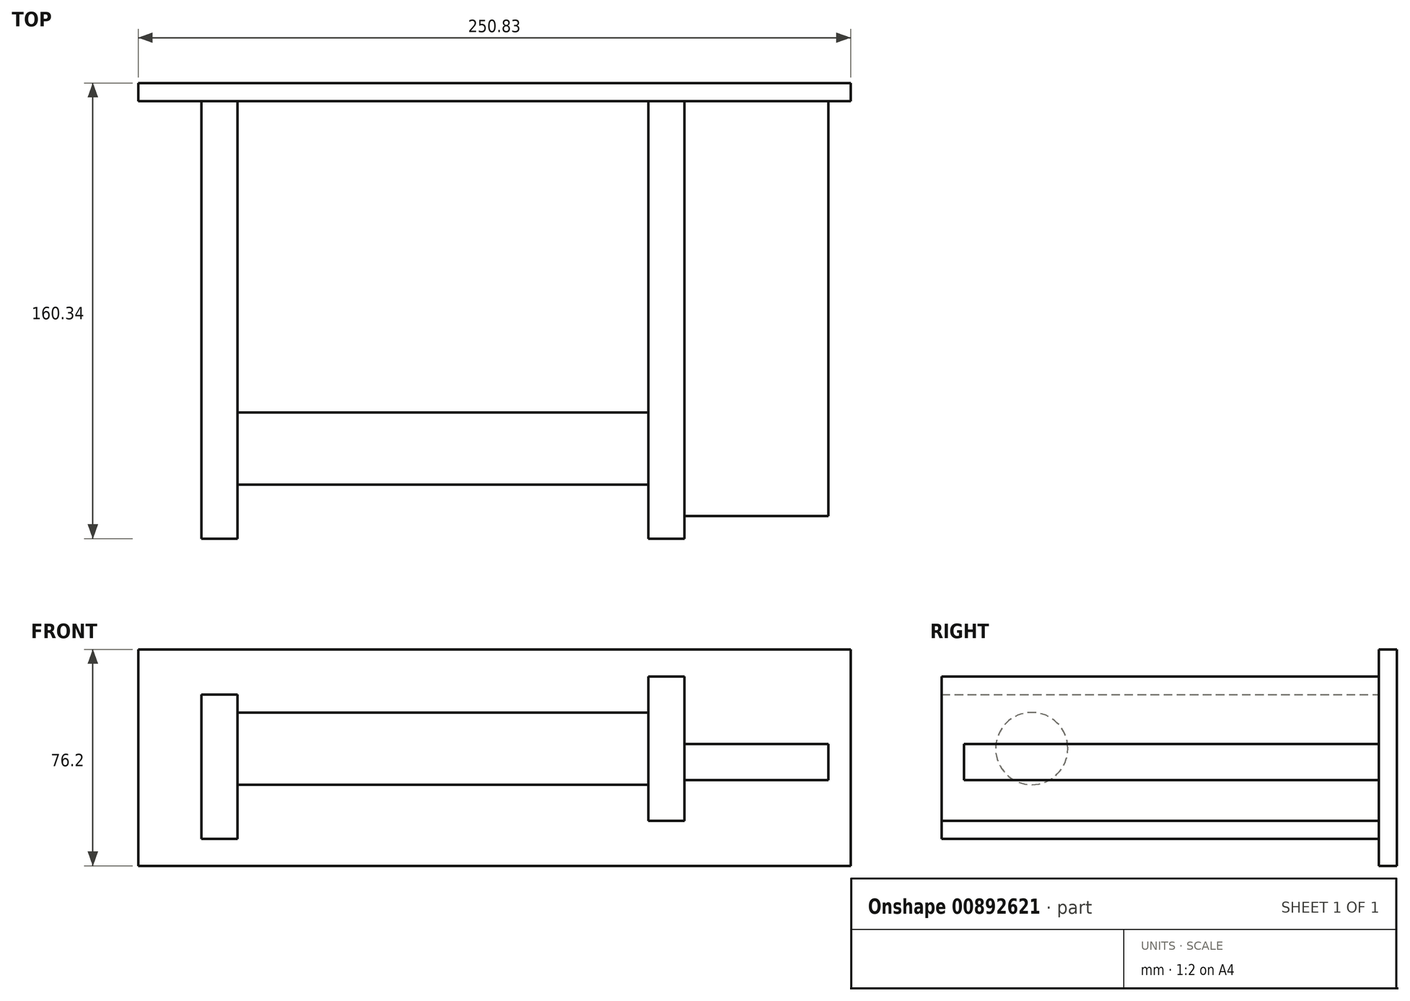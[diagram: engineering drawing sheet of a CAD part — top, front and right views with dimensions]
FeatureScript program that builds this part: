
annotation { "Feature Type Name" : "Feature", "Feature Type Description" : "" }
export const myFeature = defineFeature(function(context is Context, id is Id, definition is map)
    precondition{}
    {
        {
            var Q0;
            Q0=qCreatedBy(makeId("Front.planeOp"),FACE);
            var sketch = newSketch(context, id + "F0", { "sketchPlane" : qUnion([Q0])});
            skLineSegment(sketch, "E0.bottom", {"start": v(-131.88, 15.88) * mm, "end": v(118.95, 15.88) * mm});
            skLineSegment(sketch, "E0.top", {"start": v(-131.88, -60.33) * mm, "end": v(118.95, -60.33) * mm});
            skLineSegment(sketch, "E0.left", {"start": v(-131.88, 15.88) * mm, "end": v(-131.88, -60.33) * mm});
            skLineSegment(sketch, "E0.right", {"start": v(118.95, 15.88) * mm, "end": v(118.95, -60.33) * mm});
            skLineSegment(sketch, "E1.bottom", {"start": v(-109.65, -50.8) * mm, "end": v(-96.95, -50.8) * mm});
            skLineSegment(sketch, "E1.top", {"start": v(-109.65, 0) * mm, "end": v(-96.95, 0) * mm});
            skLineSegment(sketch, "E1.left", {"start": v(-109.65, -50.8) * mm, "end": v(-109.65, 0) * mm});
            skLineSegment(sketch, "E1.right", {"start": v(-96.95, -50.8) * mm, "end": v(-96.95, 0) * mm});
            skSolve(sketch);
        }
        {
            var Q0;
            Q0=makeQuery(id+"F0.imprint","IMPRINT",FACE,{"disambiguationData":[TD([[makeQuery(id+"F0.imprint","IMPRINT",EDGE,{"derivedFrom":sQuery(id+"F0.wireOp",EDGE,"E0.bottom")}),-1.0]])]});
            extrude(context, id + "F1", {"entities" : qUnion([Q0]), "depth" : 6.35 * mm, "offsetDistance" : 25.4 * mm});
        }
        {
            var Q0;
            Q0=makeQuery(id+"F0.imprint","IMPRINT",FACE,{"disambiguationData":[TD([[makeQuery(id+"F0.imprint","IMPRINT",EDGE,{"derivedFrom":sQuery(id+"F0.wireOp",EDGE,"E1.bottom")}),1.0]])]});
            extrude(context, id + "F2", {"entities" : qUnion([Q0]), "operationType" : NewBodyOperationType.ADD, "depth" : 160.34 * mm, "offsetDistance" : 25.4 * mm});
        }
        {
            var Q0;
            Q0=qCreatedBy(makeId("Front.planeOp"),FACE);
            var sketch = newSketch(context, id + "F3", { "sketchPlane" : qUnion([Q0])});
            skLineSegment(sketch, "E2.bottom", {"start": v(47.68, -44.45) * mm, "end": v(60.38, -44.45) * mm});
            skLineSegment(sketch, "E2.top", {"start": v(47.68, 6.35) * mm, "end": v(60.38, 6.35) * mm});
            skLineSegment(sketch, "E2.left", {"start": v(47.68, -44.45) * mm, "end": v(47.68, 6.35) * mm});
            skLineSegment(sketch, "E2.right", {"start": v(60.38, -44.45) * mm, "end": v(60.38, 6.35) * mm});
            skSolve(sketch);
        }
        {
            var Q0;
            Q0=qSketchRegion(id+"F3",true);
            extrude(context, id + "F4", {"entities" : qUnion([Q0]), "operationType" : NewBodyOperationType.ADD, "depth" : 160.34 * mm, "offsetDistance" : 25.4 * mm});
        }
        {
            var Q0;
            Q0=qCreatedBy(makeId("Front.planeOp"),FACE);
            var sketch = newSketch(context, id + "F5", { "sketchPlane" : qUnion([Q0])});
            skLineSegment(sketch, "E3.bottom", {"start": v(111.07, -30.09) * mm, "end": v(60.27, -30.09) * mm});
            skLineSegment(sketch, "E3.top", {"start": v(111.07, -17.39) * mm, "end": v(60.27, -17.39) * mm});
            skLineSegment(sketch, "E3.left", {"start": v(111.07, -30.09) * mm, "end": v(111.07, -17.39) * mm});
            skLineSegment(sketch, "E3.right", {"start": v(60.27, -30.09) * mm, "end": v(60.27, -17.39) * mm});
            skSolve(sketch);
        }
        {
            var Q0;
            Q0=qSketchRegion(id+"F5",true);
            extrude(context, id + "F6", {"entities" : qUnion([Q0]), "operationType" : NewBodyOperationType.ADD, "depth" : 152.4 * mm, "offsetDistance" : 25.4 * mm});
        }
        {
            var Q0;
            Q0=qCreatedBy(makeId("Right.planeOp"),FACE);
            var sketch = newSketch(context, id + "F7", { "sketchPlane" : qUnion([Q0])});
            skCircle(sketch, "E4", {"center": v(-128.59, -19.05) * mm, "radius": 12.7 * mm});
            skSolve(sketch);
        }
        {
            var Q0;
            Q0=makeQuery(id+"F7.imprint","IMPRINT",FACE,{"disambiguationData":[TD([[makeQuery(id+"F7.imprint","IMPRINT",EDGE,{"derivedFrom":sQuery(id+"F7.wireOp",EDGE,"E4")}),1.0]])]});
            extrude(context, id + "F8", {"entities" : qUnion([Q0]), "operationType" : NewBodyOperationType.ADD, "depth" : 55.63 * mm, "offsetDistance" : 25.4 * mm, "hasSecondDirection" : true, "secondDirectionOppositeDirection" : true, "secondDirectionDepth" : 97.03 * mm});
        }
    });
